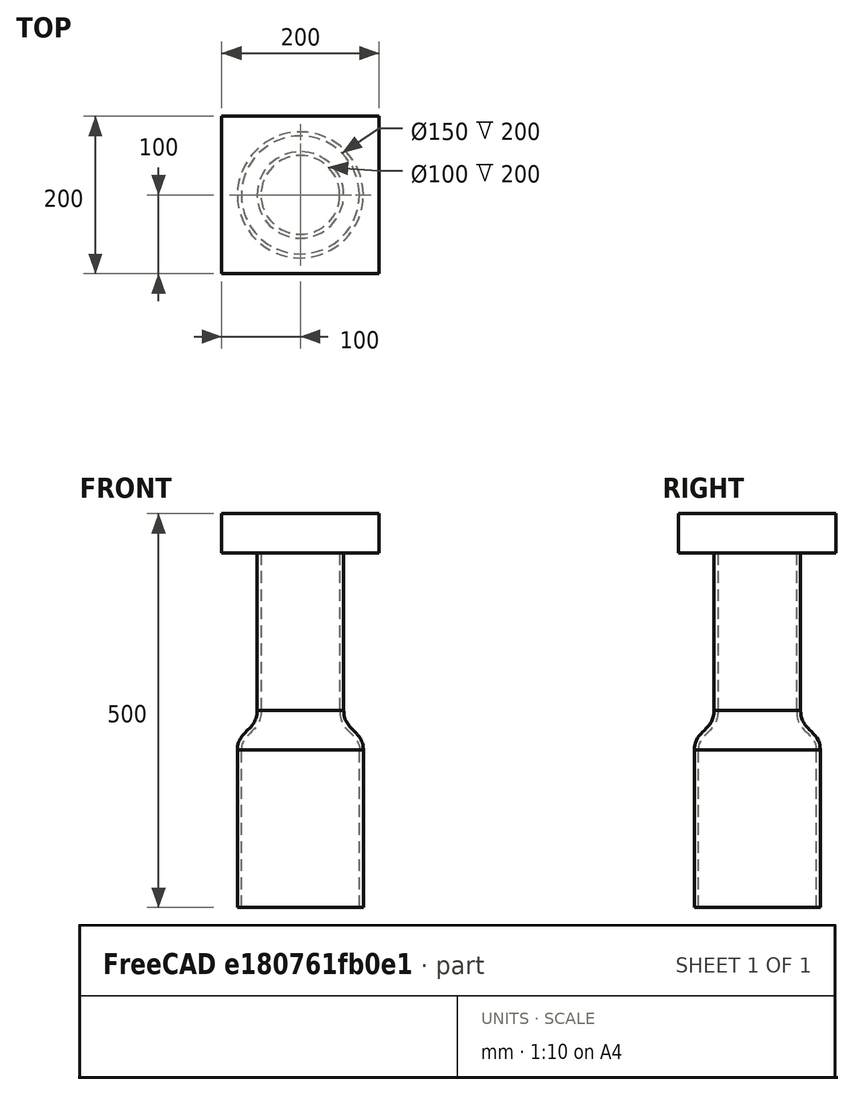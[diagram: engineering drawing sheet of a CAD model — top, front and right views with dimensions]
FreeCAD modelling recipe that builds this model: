
FCSTD DOCUMENT  (FreeCAD 0.21R33694 (Git))
Label: transition
License: All rights reserved
LicenseURL: http://en.wikipedia.org/wiki/All_rights_reserved
objects: Fem::ConstraintForce×2, Sketcher::SketchObject×2, Part::Revolution×2, Fem::FeaturePython×2, Part::Box×1, App::MaterialObjectPython×1, Fem::FemSolverObjectPython×1, Part::FeaturePython×1, Fem::ConstraintFixed×1, Fem::FemMeshObjectPython×1, Fem::FemAnalysis×1
note: 6 computed .brp shape members not serialized (recipe doc carries the construction recipe); baked Part::Feature solids carry a one-line shape summary decoded from their .brp

FEATURE [Part::Box] Box  label="Cube"
  AttacherType = Attacher::AttachEngine3D
  Height = 50
  Length = 200
  Placement = pos=(-100,-100,250) rot=(0,0,1;0rad)
  Width = 200
FEATURE [Fem::ConstraintForce] ConstraintForce
  Direction = -> Box [Edge1]
  DirectionVector = (0,0,1)
  Force = 1000
  NormalDirection = (-1,0,0)
  Points = (16) [(-100,100,250),(-100,100,266.667),(-100,100,283.333),(-100,100,300),(-100,33.3333,250),(-100,33.3333,266.667),(-100,33.3333,283.333),+9 more]
  References = -> [Box]
  Scale = 11
FEATURE [Fem::ConstraintForce] ConstraintForce001
  Direction = -> Box [Edge5]
  DirectionVector = (0,0,-1)
  Force = 1000
  NormalDirection = (1,0,0)
  Points = (16) [(100,100,250),(100,100,266.667),(100,100,283.333),(100,100,300),(100,33.3333,250),(100,33.3333,266.667),(100,33.3333,283.333),(100,33.3333,300),+8 more]
  References = -> [Box]
  Reversed = true
  Scale = 11
FEATURE [App::MaterialObjectPython] MaterialSolid  # material (typed FeaturePython)
  Category = 0
  Material = AuthorAndLicense=(c) 2014 M. Münch - GNU Lesser General Public License (LGPL),CardName=Steel-St-E-315,Density=7800 kg/m^3,Father=Metal,+13 more (map truncated)
FEATURE [Fem::FemSolverObjectPython] SolverCcxTools  # FEM object (typed FeaturePython)
  AnalysisType = 0
  BeamShellResultOutput3D = false
  BucklingFactors = 1
  EigenmodeHighLimit = 1000000
  EigenmodeLowLimit = 0
  EigenmodesCount = 10
  GeometricalNonlinearity = 0
  IterationsControlParameterCutb = 0.25,0.5,0.75,0.85,,,1.5,
  IterationsControlParameterIter = 4,8,9,200,10,400,,200,,
  IterationsControlParameterTimeUse = false
  IterationsThermoMechMaximum = 2000
  IterationsUserDefinedIncrementations = false
  IterationsUserDefinedTimeStepLength = false
  MaterialNonlinearity = 0
  MatrixSolverType = 0
  SplitInputWriter = false
  ThermoMechSteadyState = true
  TimeEnd = 1
  TimeInitialStep = 0.01
FEATURE [Sketcher::SketchObject] Sketch001
  FullyConstrained = false
  MapMode = 5
  Placement = pos=(0,0,0) rot=(1,0,0;1.5708rad)
  sketch-geometry (25):
    g0: LineSegment StartX=0 StartY=25 StartZ=0 EndX=100 EndY=25 EndZ=0
    g1: LineSegment StartX=50 StartY=50 StartZ=0 EndX=50 EndY=25 EndZ=0
    g2: LineSegment StartX=55 StartY=50 StartZ=0 EndX=55 EndY=25 EndZ=0
    g3: LineSegment StartX=75 StartY=0 StartZ=0 EndX=75 EndY=25 EndZ=0
    g4: LineSegment StartX=80 StartY=0 StartZ=0 EndX=80 EndY=25 EndZ=0
    g5-g9: Circle x5 (B-spline internal-alignment scaffolding for g10; pole/knot coordinates omitted)
    g10: BSplineCurve PolesCount=5 KnotsCount=3 Degree=3 IsPeriodic=0
    g11: GeomPoint X=50 Y=50 Z=0
    g12: GeomPoint X=60 Y=25 Z=0
    g13: GeomPoint X=75 Y=0 Z=0
    g14-g18: Circle x5 (B-spline internal-alignment scaffolding for g19; pole/knot coordinates omitted)
    g19: BSplineCurve PolesCount=5 KnotsCount=3 Degree=3 IsPeriodic=0
    g20: GeomPoint X=55 Y=50 Z=0
    g21: GeomPoint X=67.07 Y=25 Z=0
    g22: GeomPoint X=80 Y=0 Z=0
    g23: LineSegment StartX=50 StartY=50 StartZ=0 EndX=55 EndY=50 EndZ=0
    g24: LineSegment StartX=75 StartY=0 StartZ=0 EndX=80 EndY=0 EndZ=0
  constraints (57):
    c: DistanceY(g-1,g10) = 50
    c: DistanceX(g-1,g10) = 50
    c: PointOnObject(g0,g-2)
    c: Horizontal(g0)
    c: DistanceY(g-1,g0) = 25
    c: DistanceX(g-1,g0) = 100
    c: Vertical(g1)
    c: Vertical(g2)
    c: Vertical(g3)
    c: Vertical(g4)
    c: Weight(g5) = 1
    c: Equal(g5,g6)
    c: PointOnObject(g6,g1)
    c: Equal(g5,g7)
    c: PointOnObject(g7,g0)
    c: Equal(g5,g8)
    c: PointOnObject(g8,g3)
    c: Equal(g5,g9)
    c: InternalAlignment(g5-g9 -> g10) x5
    c: InternalAlignment(g11,g10)
    c: InternalAlignment(g12,g10)
    c: InternalAlignment(g13,g10)
    c: Weight(g14) = 1
    c: Equal(g14,g15)
    c: PointOnObject(g15,g2)
    c: Equal(g14,g16)
    c: PointOnObject(g16,g0)
    c: Equal(g14,g17)
    c: PointOnObject(g17,g4)
    c: Equal(g14,g18)
    c: InternalAlignment(g14-g18 -> g19) x5
    c: InternalAlignment(g20,g19)
    c: InternalAlignment(g21,g19)
    c: InternalAlignment(g22,g19)
    c: PointOnObject(g21,g0)
    c: PointOnObject(g12,g0)
    c: DistanceY(g17,g8) = 0
    c: PointOnObject(g1,g0)
    c: PointOnObject(g2,g0)
    c: PointOnObject(g3,g0)
    c: PointOnObject(g4,g0)
    c: DistanceX(g12,g21) = 7.07
    c: Coincident(g23,g10)
    c: Coincident(g23,g19)
    c: Horizontal(g23)
    c: Coincident(g24,g10)
    c: Coincident(g24,g19)
    c: Horizontal(g24)
    c: DistanceX(g23,g23) = 5
    c: DistanceX(g24,g24) = 5
    c: PointOnObject(g19,g-1)
    c: Coincident(g1,g10)
    c: Coincident(g2,g19)
    c: Coincident(g3,g10)
    c: Coincident(g4,g19)
    c: DistanceX(g-1,g10) = 75
    c: DistanceX(g-1,g12) = 60
FEATURE [Sketcher::SketchObject] Sketch
  ExternalGeometry = -> [Sketch001]
  FullyConstrained = true
  MapMode = 2
  Placement = pos=(0,0,0) rot=(1,0,0;1.5708rad)
  Support = -> [Sketch001]
  sketch-geometry (8):
    g0: LineSegment StartX=50 StartY=50 StartZ=0 EndX=55 EndY=50 EndZ=0
    g1: LineSegment StartX=55 StartY=50 StartZ=0 EndX=55 EndY=250 EndZ=0
    g2: LineSegment StartX=55 StartY=250 StartZ=0 EndX=50 EndY=250 EndZ=0
    g3: LineSegment StartX=50 StartY=250 StartZ=0 EndX=50 EndY=50 EndZ=0
    g4: LineSegment StartX=75 StartY=0 StartZ=0 EndX=80 EndY=0 EndZ=0
    g5: LineSegment StartX=80 StartY=0 StartZ=0 EndX=80 EndY=-200 EndZ=0
    g6: LineSegment StartX=80 StartY=-200 StartZ=0 EndX=75 EndY=-200 EndZ=0
    g7: LineSegment StartX=75 StartY=-200 StartZ=0 EndX=75 EndY=0 EndZ=0
  constraints (22):
    c: Coincident(g0,g1)
    c: Coincident(g1,g2)
    c: Coincident(g2,g3)
    c: Coincident(g3,g0)
    c: Horizontal(g0)
    c: Horizontal(g2)
    c: Vertical(g1)
    c: Vertical(g3)
    c: Coincident(g0,g-3)
    c: DistanceX(g0,g0) = 5
    c: DistanceY(g1,g1) = 200
    c: Coincident(g4,g5)
    c: Coincident(g5,g6)
    c: Coincident(g6,g7)
    c: Coincident(g7,g4)
    c: Horizontal(g4)
    c: Horizontal(g6)
    c: Vertical(g5)
    c: Vertical(g7)
    c: Coincident(g4,g-4)
    c: DistanceX(g4,g4) = 5
    c: DistanceY(g5,g5) = 200
FEATURE [Part::Revolution] Revolve
  Angle = 360
  Axis = (0,0,1)
  Base = (0,0,0)
  FaceMakerClass = Part::FaceMakerBullseye
  Solid = true
  Source = -> Sketch001
  Symmetric = false
FEATURE [Part::Revolution] Revolve001
  Angle = 360
  Axis = (0,0,1)
  Base = (0,0,0)
  FaceMakerClass = Part::FaceMakerBullseye
  Solid = true
  Source = -> Sketch
  Symmetric = false
FEATURE [Part::FeaturePython] BooleanFragments  # WARN: FeaturePython — macro-defined, semantics opaque (R4)
  Mode = 2
  Objects = -> [Box,Revolve,Revolve001]
  Tolerance = 0
FEATURE [Fem::ConstraintFixed] ConstraintFixed
  NormalDirection = (0,0,-1)
  References = -> [BooleanFragments]
  Scale = 13
FEATURE [Fem::FeaturePython] MeshRegion  # FEM object (typed FeaturePython)
  CharacteristicLength = 10
  References = -> [BooleanFragments]
FEATURE [Fem::FeaturePython] MeshRegion001  # FEM object (typed FeaturePython)
  CharacteristicLength = 100
  References = -> [BooleanFragments]
FEATURE [Fem::FemMeshObjectPython] FEMMeshGmsh  # FEM object (typed FeaturePython)
  Algorithm2D = 0
  Algorithm3D = 0
  CharacteristicLengthMax = 50
  CharacteristicLengthMin = 0
  CoherenceMesh = true
  ElementDimension = 0
  ElementOrder = 1
  GeometryTolerance = 1e-06
  GroupsOfNodes = false
  HighOrderOptimize = 0
  MeshRegionList = -> [MeshRegion,MeshRegion001]
  MeshSizeFromCurvature = 12
  OptimizeNetgen = false
  OptimizeStd = true
  Part = -> BooleanFragments
  RecombinationAlgorithm = 0
  Recombine3DAll = false
  RecombineAll = false
  SecondOrderLinear = false
FEATURE [Fem::FemAnalysis] Analysis
  Group = -> [ConstraintFixed,ConstraintForce,ConstraintForce001,MaterialSolid,SolverCcxTools,FEMMeshGmsh]
